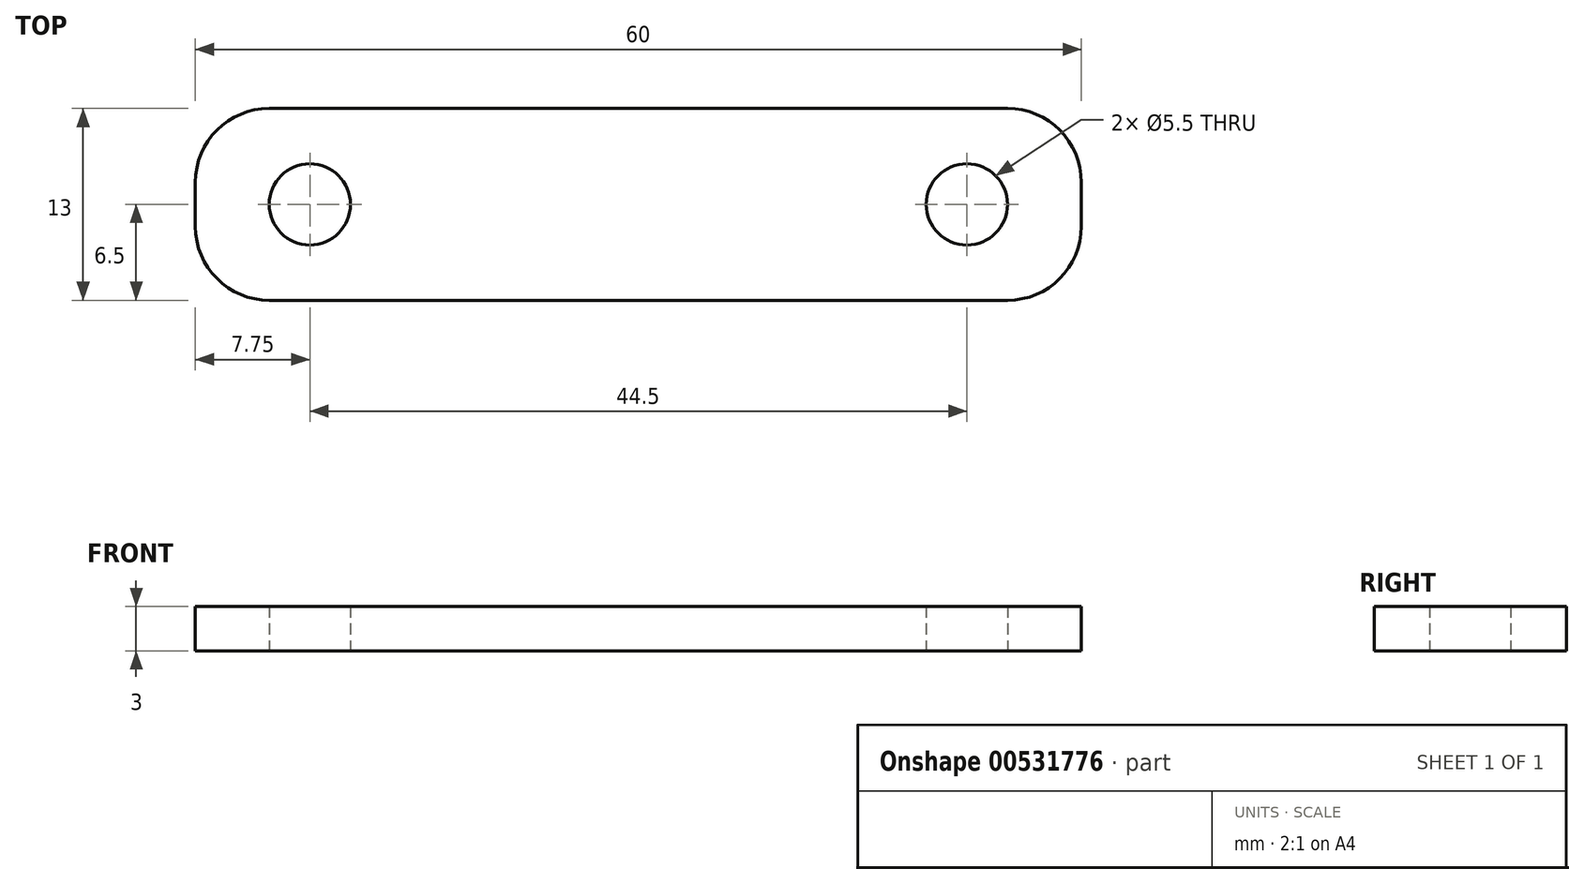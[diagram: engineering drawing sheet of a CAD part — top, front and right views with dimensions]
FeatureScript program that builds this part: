
annotation { "Feature Type Name" : "Feature", "Feature Type Description" : "" }
export const myFeature = defineFeature(function(context is Context, id is Id, definition is map)
    precondition{}
    {
        {
            var Q0;
            Q0=qCreatedBy(makeId("Top.planeOp"),FACE);
            var sketch = newSketch(context, id + "F0", { "sketchPlane" : qUnion([Q0])});
            skLineSegment(sketch, "E0.bottom", {"start": v(25, -6.5) * mm, "end": v(-25, -6.5) * mm});
            skLineSegment(sketch, "E0.top", {"start": v(25, 6.5) * mm, "end": v(-25, 6.5) * mm});
            skLineSegment(sketch, "E0.left", {"start": v(30, -1.5) * mm, "end": v(30, 1.5) * mm});
            skLineSegment(sketch, "E0.right", {"start": v(-30, -1.5) * mm, "end": v(-30, 1.5) * mm});
            skPoint(sketch, "E0.middle", {"position": v(0, 0) * mm});
            skLineSegment(sketch, "E1", {"start": v(-30, 0) * mm, "end": v(30, 0) * mm});
            skCircle(sketch, "E2", {"center": v(22.25, 0) * mm, "radius": 2.75 * mm});
            skCircle(sketch, "E3", {"center": v(-22.25, 0) * mm, "radius": 2.75 * mm});
            skPoint(sketch, "E4.visualSharp", {"position": v(30, 6.5) * mm});
            skArc(sketch, "E4.filletArc", {"start": v(30, 1.5) * mm, "mid": v(28.54, 5.04) * mm, "end": v(25, 6.5) * mm});
            skPoint(sketch, "E5.visualSharp", {"position": v(30, -6.5) * mm});
            skArc(sketch, "E5.filletArc", {"start": v(25, -6.5) * mm, "mid": v(28.54, -5.04) * mm, "end": v(30, -1.5) * mm});
            skPoint(sketch, "E6.visualSharp", {"position": v(-30, 6.5) * mm});
            skArc(sketch, "E6.filletArc", {"start": v(-25, 6.5) * mm, "mid": v(-28.54, 5.04) * mm, "end": v(-30, 1.5) * mm});
            skPoint(sketch, "E7.visualSharp", {"position": v(-30, -6.5) * mm});
            skArc(sketch, "E7.filletArc", {"start": v(-30, -1.5) * mm, "mid": v(-28.54, -5.04) * mm, "end": v(-25, -6.5) * mm});
            skSolve(sketch);
        }
        {
            var Q0;
            Q0 = qSketchRegion(id + "F0", true);
            extrude(context, id + "F1", {"entities" : qUnion([Q0]), "depth" : 3 * mm, "offsetDistance" : 25 * mm});
        }
    });
